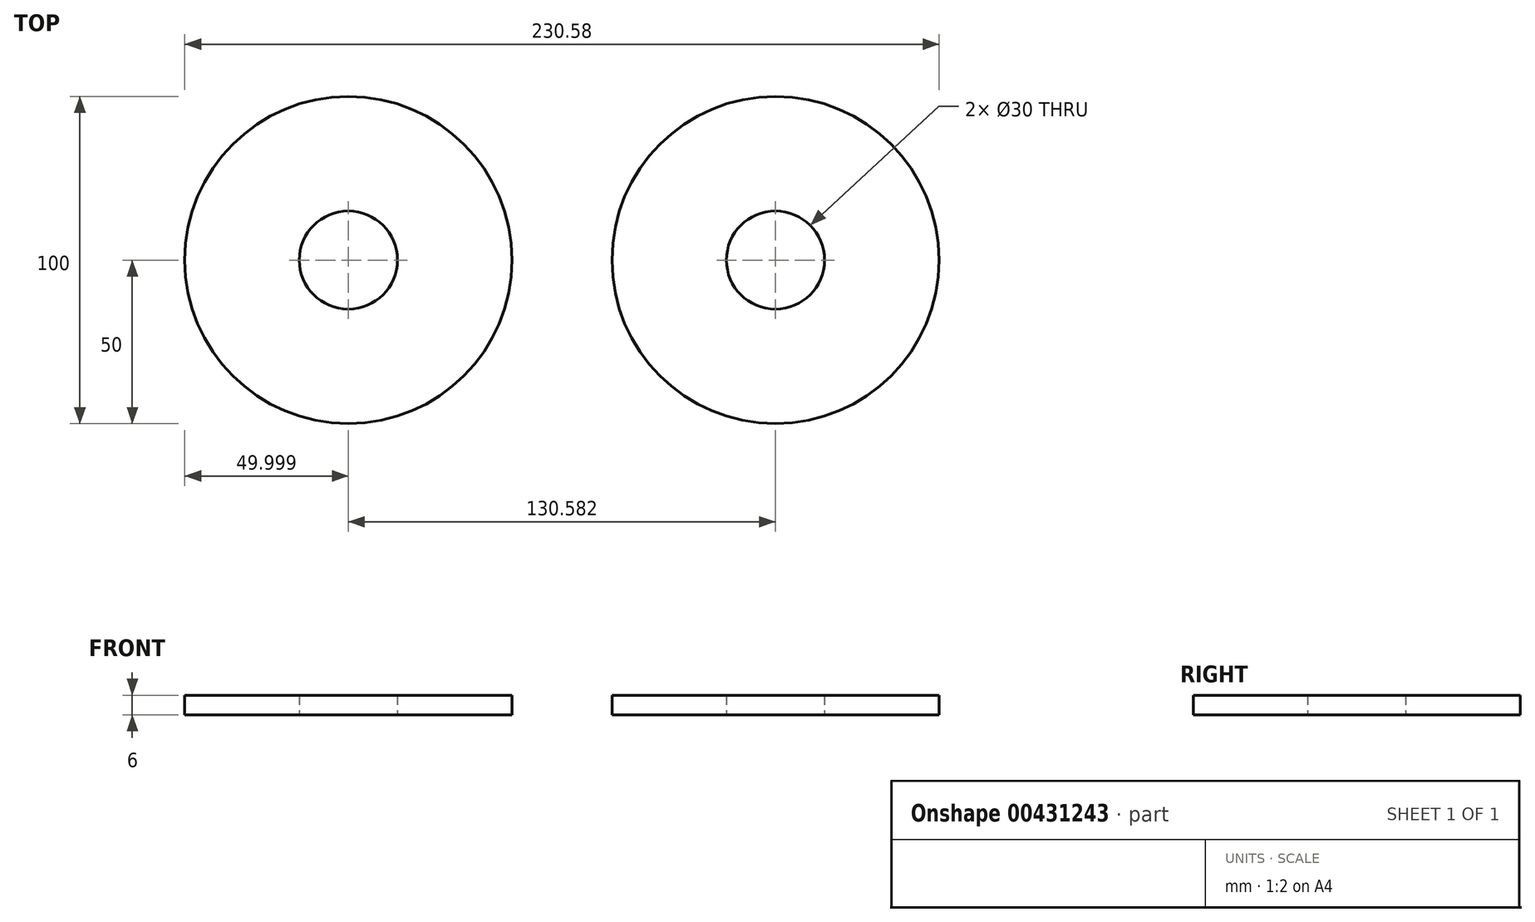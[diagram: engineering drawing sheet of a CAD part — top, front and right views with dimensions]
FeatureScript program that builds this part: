
annotation { "Feature Type Name" : "Feature", "Feature Type Description" : "" }
export const myFeature = defineFeature(function(context is Context, id is Id, definition is map)
    precondition{}
    {
        {
            var Q0;
            Q0=qCreatedBy(makeId("Top.planeOp"),FACE);
            var sketch = newSketch(context, id + "F0", { "sketchPlane" : qUnion([Q0])});
            skCircle(sketch, "E0", {"center": v(0, 0) * mm, "radius": 50 * mm});
            skCircle(sketch, "E1", {"center": v(0, 0) * mm, "radius": 15 * mm});
            skCircle(sketch, "E2.MirrorC", {"center": v(-130.58, 0) * mm, "radius": 15 * mm});
            skCircle(sketch, "E3.MirrorC", {"center": v(-130.58, 0) * mm, "radius": 50 * mm});
            skSolve(sketch);
        }
        {
            var Q0;
            Q0 = qSketchRegion(id + "F0", true);
            extrude(context, id + "F1", {"entities" : qUnion([Q0]), "depth" : 6 * mm});
        }
    });
